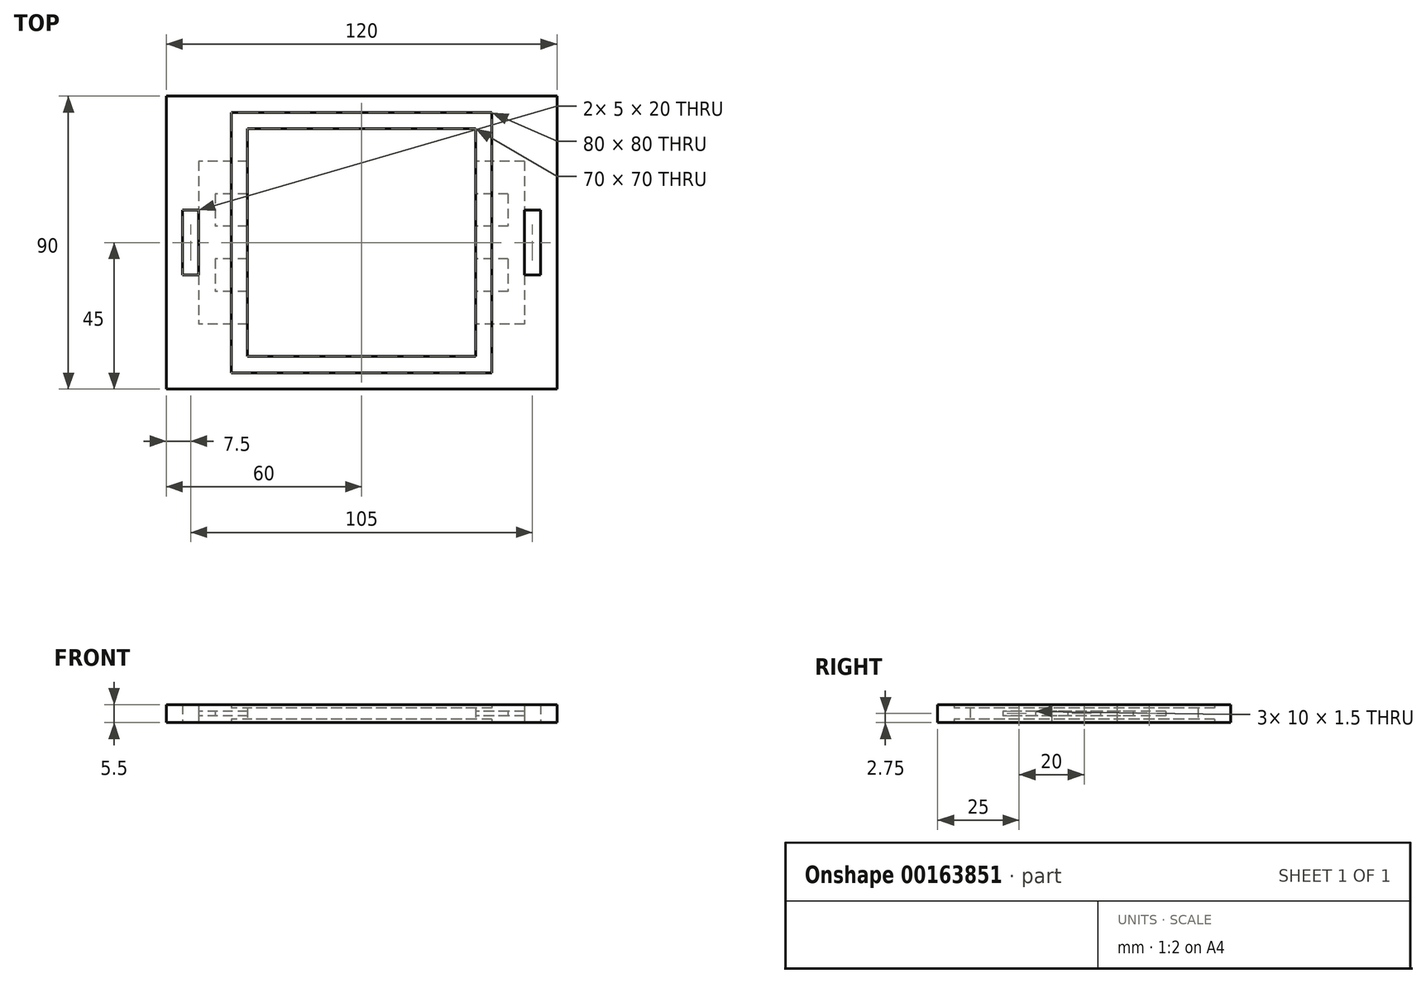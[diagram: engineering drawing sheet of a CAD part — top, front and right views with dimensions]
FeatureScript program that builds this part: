
annotation { "Feature Type Name" : "Feature", "Feature Type Description" : "" }
export const myFeature = defineFeature(function(context is Context, id is Id, definition is map)
    precondition{}
    {
        {
            var Q0;
            Q0=qCreatedBy(makeId("Top.planeOp"),FACE);
            var sketch = newSketch(context, id + "F0", { "sketchPlane" : qUnion([Q0])});
            skLineSegment(sketch, "E0.bottom", {"start": v(60, 45) * mm, "end": v(-60, 45) * mm});
            skLineSegment(sketch, "E0.top", {"start": v(60, -45) * mm, "end": v(-60, -45) * mm});
            skLineSegment(sketch, "E0.left", {"start": v(60, 45) * mm, "end": v(60, -45) * mm});
            skLineSegment(sketch, "E0.right", {"start": v(-60, 45) * mm, "end": v(-60, -45) * mm});
            skPoint(sketch, "E0.middle", {"position": v(0, 0) * mm});
            skLineSegment(sketch, "E1.bottom", {"start": v(35, 35) * mm, "end": v(-35, 35) * mm});
            skLineSegment(sketch, "E1.top", {"start": v(35, -35) * mm, "end": v(-35, -35) * mm});
            skLineSegment(sketch, "E1.left", {"start": v(35, 35) * mm, "end": v(35, -35) * mm});
            skLineSegment(sketch, "E1.right", {"start": v(-35, 35) * mm, "end": v(-35, -35) * mm});
            skLineSegment(sketch, "E2.bottom", {"start": v(40, 40) * mm, "end": v(-40, 40) * mm});
            skLineSegment(sketch, "E2.top", {"start": v(40, -40) * mm, "end": v(-40, -40) * mm});
            skLineSegment(sketch, "E2.left", {"start": v(40, 40) * mm, "end": v(40, -40) * mm});
            skLineSegment(sketch, "E2.right", {"start": v(-40, 40) * mm, "end": v(-40, -40) * mm});
            skLineSegment(sketch, "E3.0", {"start": v(50, 25) * mm, "end": v(35, 25) * mm});
            skLineSegment(sketch, "E4.0", {"start": v(50, -25) * mm, "end": v(35, -25) * mm});
            skLineSegment(sketch, "E5.trimOffspring", {"start": v(-35, 25) * mm, "end": v(-50, 25) * mm});
            skLineSegment(sketch, "E6.trimOffspring", {"start": v(-35, -25) * mm, "end": v(-50, -25) * mm});
            skLineSegment(sketch, "E7.0", {"start": v(-35, 15) * mm, "end": v(-45, 15) * mm});
            skLineSegment(sketch, "E8.0", {"start": v(-35, -15) * mm, "end": v(-45, -15) * mm});
            skLineSegment(sketch, "E9.0", {"start": v(-35, -5) * mm, "end": v(-45, -5) * mm});
            skLineSegment(sketch, "E10.0", {"start": v(-35, 5) * mm, "end": v(-45, 5) * mm});
            skLineSegment(sketch, "E11.0", {"start": v(45, 15) * mm, "end": v(35, 15) * mm});
            skLineSegment(sketch, "E12.0", {"start": v(45, 5) * mm, "end": v(35, 5) * mm});
            skLineSegment(sketch, "E13.0", {"start": v(45, -15) * mm, "end": v(35, -15) * mm});
            skLineSegment(sketch, "E14.0", {"start": v(45, -5) * mm, "end": v(35, -5) * mm});
            skLineSegment(sketch, "E15.0", {"start": v(-50, 25) * mm, "end": v(-50, -25) * mm});
            skLineSegment(sketch, "E16.0", {"start": v(-45, 15) * mm, "end": v(-45, 5) * mm});
            skLineSegment(sketch, "E17.0", {"start": v(50, 25) * mm, "end": v(50, -25) * mm});
            skLineSegment(sketch, "E18.0", {"start": v(45, 15) * mm, "end": v(45, 5) * mm});
            skLineSegment(sketch, "E19.0", {"start": v(55, -10) * mm, "end": v(50, -10) * mm});
            skLineSegment(sketch, "E20.0", {"start": v(55, 10) * mm, "end": v(50, 10) * mm});
            skLineSegment(sketch, "E21.trimOffspring", {"start": v(-50, 10) * mm, "end": v(-55, 10) * mm});
            skLineSegment(sketch, "E22.trimOffspring", {"start": v(-50, -10) * mm, "end": v(-55, -10) * mm});
            skLineSegment(sketch, "E23.0", {"start": v(-55, 10) * mm, "end": v(-55, -10) * mm});
            skLineSegment(sketch, "E24.0", {"start": v(55, 10) * mm, "end": v(55, -10) * mm});
            skLineSegment(sketch, "E25.trimOffspring", {"start": v(45, -5) * mm, "end": v(45, -15) * mm});
            skLineSegment(sketch, "E26.trimOffspring", {"start": v(-45, -5) * mm, "end": v(-45, -15) * mm});
            skSolve(sketch);
        }
        {
            var Q0;
            Q0=makeQuery(id+"F0.imprint","IMPRINT",FACE,{"disambiguationData":[TD([[makeQuery(id+"F0.imprint","IMPRINT",EDGE,{"derivedFrom":sQuery(id+"F0.wireOp",EDGE,"E0.bottom")}),1.0]])]});
            var Q1;
            {var subQ0=sQuery(id+"F0.wireOp",EDGE,"E16.0");Q1=makeQuery(id+"F0.imprint","IMPRINT",FACE,{"disambiguationData":[TD([[makeQuery(id+"F0.imprint","IMPRINT",EDGE,{"derivedFrom":subQ0}),-1.0]])]});}
            var Q2;
            {var subQ4=sQuery(id+"F0.wireOp",EDGE,"E18.0");Q2=makeQuery(id+"F0.imprint","IMPRINT",FACE,{"disambiguationData":[TD([[makeQuery(id+"F0.imprint","IMPRINT",EDGE,{"derivedFrom":subQ4}),1.0]])]});}
            var Q3;
            {var subQ5=sQuery(id+"F0.wireOp",EDGE,"E18.0");Q3=makeQuery(id+"F0.imprint","IMPRINT",FACE,{"disambiguationData":[TD([[makeQuery(id+"F0.imprint","IMPRINT",EDGE,{"derivedFrom":subQ5}),-1.0]])]});}
            var Q4;
            {var subQ5=sQuery(id+"F0.wireOp",EDGE,"E25.trimOffspring");Q4=makeQuery(id+"F0.imprint","IMPRINT",FACE,{"disambiguationData":[TD([[makeQuery(id+"F0.imprint","IMPRINT",EDGE,{"derivedFrom":subQ5}),-1.0]])]});}
            var Q5;
            {var subQ5=sQuery(id+"F0.wireOp",EDGE,"E26.trimOffspring");Q5=makeQuery(id+"F0.imprint","IMPRINT",FACE,{"disambiguationData":[TD([[makeQuery(id+"F0.imprint","IMPRINT",EDGE,{"derivedFrom":subQ5}),1.0]])]});}
            var Q6;
            {var subQ5=sQuery(id+"F0.wireOp",EDGE,"E16.0");Q6=makeQuery(id+"F0.imprint","IMPRINT",FACE,{"disambiguationData":[TD([[makeQuery(id+"F0.imprint","IMPRINT",EDGE,{"derivedFrom":subQ5}),1.0]])]});}
            extrude(context, id + "F1", {"entities" : qUnion([Q0, Q1, Q2, Q3, Q4, Q5, Q6]), "depth" : 2 * mm});
        }
        {
            var Q0;
            Q0=makeQuery(id+"F0.imprint","IMPRINT",FACE,{"disambiguationData":[TD([[makeQuery(id+"F0.imprint","IMPRINT",EDGE,{"derivedFrom":sQuery(id+"F0.wireOp",EDGE,"E0.bottom")}),1.0]])]});
            var Q1;
            {var subQ5=sQuery(id+"F0.wireOp",EDGE,"E26.trimOffspring");Q1=makeQuery(id+"F0.imprint","IMPRINT",FACE,{"disambiguationData":[TD([[makeQuery(id+"F0.imprint","IMPRINT",EDGE,{"derivedFrom":subQ5}),1.0]])]});}
            var Q2;
            {var subQ5=sQuery(id+"F0.wireOp",EDGE,"E16.0");Q2=makeQuery(id+"F0.imprint","IMPRINT",FACE,{"disambiguationData":[TD([[makeQuery(id+"F0.imprint","IMPRINT",EDGE,{"derivedFrom":subQ5}),1.0]])]});}
            var Q3;
            {var subQ5=sQuery(id+"F0.wireOp",EDGE,"E18.0");Q3=makeQuery(id+"F0.imprint","IMPRINT",FACE,{"disambiguationData":[TD([[makeQuery(id+"F0.imprint","IMPRINT",EDGE,{"derivedFrom":subQ5}),-1.0]])]});}
            var Q4;
            {var subQ5=sQuery(id+"F0.wireOp",EDGE,"E25.trimOffspring");Q4=makeQuery(id+"F0.imprint","IMPRINT",FACE,{"disambiguationData":[TD([[makeQuery(id+"F0.imprint","IMPRINT",EDGE,{"derivedFrom":subQ5}),-1.0]])]});}
            extrude(context, id + "F2", {"entities" : qUnion([Q0, Q1, Q2, Q3, Q4]), "operationType" : NewBodyOperationType.ADD, "depth" : 3.5 * mm, "hasSecondDirection" : true, "secondDirectionOppositeDirection" : false, "secondDirectionDepth" : 2 * mm});
        }
        {
            var Q0;
            Q0=makeQuery(id+"F0.imprint","IMPRINT",FACE,{"disambiguationData":[TD([[makeQuery(id+"F0.imprint","IMPRINT",EDGE,{"derivedFrom":sQuery(id+"F0.wireOp",EDGE,"E0.bottom")}),1.0]])]});
            var Q1;
            {var subQ0=sQuery(id+"F0.wireOp",EDGE,"E16.0");Q1=makeQuery(id+"F0.imprint","IMPRINT",FACE,{"disambiguationData":[TD([[makeQuery(id+"F0.imprint","IMPRINT",EDGE,{"derivedFrom":subQ0}),-1.0]])]});}
            var Q2;
            {var subQ4=sQuery(id+"F0.wireOp",EDGE,"E18.0");Q2=makeQuery(id+"F0.imprint","IMPRINT",FACE,{"disambiguationData":[TD([[makeQuery(id+"F0.imprint","IMPRINT",EDGE,{"derivedFrom":subQ4}),1.0]])]});}
            var Q3;
            {var subQ5=sQuery(id+"F0.wireOp",EDGE,"E18.0");Q3=makeQuery(id+"F0.imprint","IMPRINT",FACE,{"disambiguationData":[TD([[makeQuery(id+"F0.imprint","IMPRINT",EDGE,{"derivedFrom":subQ5}),-1.0]])]});}
            var Q4;
            {var subQ5=sQuery(id+"F0.wireOp",EDGE,"E25.trimOffspring");Q4=makeQuery(id+"F0.imprint","IMPRINT",FACE,{"disambiguationData":[TD([[makeQuery(id+"F0.imprint","IMPRINT",EDGE,{"derivedFrom":subQ5}),-1.0]])]});}
            var Q5;
            {var subQ5=sQuery(id+"F0.wireOp",EDGE,"E26.trimOffspring");Q5=makeQuery(id+"F0.imprint","IMPRINT",FACE,{"disambiguationData":[TD([[makeQuery(id+"F0.imprint","IMPRINT",EDGE,{"derivedFrom":subQ5}),1.0]])]});}
            var Q6;
            {var subQ5=sQuery(id+"F0.wireOp",EDGE,"E16.0");Q6=makeQuery(id+"F0.imprint","IMPRINT",FACE,{"disambiguationData":[TD([[makeQuery(id+"F0.imprint","IMPRINT",EDGE,{"derivedFrom":subQ5}),1.0]])]});}
            extrude(context, id + "F3", {"entities" : qUnion([Q0, Q1, Q2, Q3, Q4, Q5, Q6]), "operationType" : NewBodyOperationType.ADD, "depth" : 5.5 * mm, "hasSecondDirection" : true, "secondDirectionOppositeDirection" : false, "secondDirectionDepth" : 3.5 * mm});
        }
        {
            var Q0;
            {var subQ1=sQuery(id+"F0.wireOp",EDGE,"E1.top");Q0=makeQuery(id+"F0.imprint","IMPRINT",FACE,{"disambiguationData":[TD([[makeQuery(id+"F0.imprint","IMPRINT",EDGE,{"derivedFrom":subQ1}),1.0]])]});}
            var Q1;
            {var subQ0=sQuery(id+"F0.wireOp",EDGE,"E6.trimOffspring");var subQ1=sQuery(id+"F0.wireOp",EDGE,"E1.right");var subQ2=makeQuery(id+"F0.imprint","INTERSECT",VERTEX,{"derivedFrom":[subQ1,subQ0]});Q1=makeQuery(id+"F0.imprint","IMPRINT",FACE,{"disambiguationData":[TD([[makeQuery(id+"F0.imprint","IMPRINT",EDGE,{"disambiguationData":[TD([[subQ2,1.0]])],"derivedFrom":subQ1}),-1.0]])]});}
            var Q2;
            {var subQ0=sQuery(id+"F0.wireOp",EDGE,"E8.0");var subQ1=sQuery(id+"F0.wireOp",EDGE,"E1.right");var subQ2=makeQuery(id+"F0.imprint","INTERSECT",VERTEX,{"derivedFrom":[subQ1,subQ0]});Q2=makeQuery(id+"F0.imprint","IMPRINT",FACE,{"disambiguationData":[TD([[makeQuery(id+"F0.imprint","IMPRINT",EDGE,{"disambiguationData":[TD([[subQ2,1.0]])],"derivedFrom":subQ1}),-1.0]])]});}
            var Q3;
            {var subQ0=sQuery(id+"F0.wireOp",EDGE,"E9.0");var subQ1=sQuery(id+"F0.wireOp",EDGE,"E1.right");var subQ2=makeQuery(id+"F0.imprint","INTERSECT",VERTEX,{"derivedFrom":[subQ1,subQ0]});Q3=makeQuery(id+"F0.imprint","IMPRINT",FACE,{"disambiguationData":[TD([[makeQuery(id+"F0.imprint","IMPRINT",EDGE,{"disambiguationData":[TD([[subQ2,1.0]])],"derivedFrom":subQ1}),-1.0]])]});}
            var Q4;
            {var subQ0=sQuery(id+"F0.wireOp",EDGE,"E7.0");var subQ1=sQuery(id+"F0.wireOp",EDGE,"E1.right");var subQ2=makeQuery(id+"F0.imprint","INTERSECT",VERTEX,{"derivedFrom":[subQ1,subQ0]});Q4=makeQuery(id+"F0.imprint","IMPRINT",FACE,{"disambiguationData":[TD([[makeQuery(id+"F0.imprint","IMPRINT",EDGE,{"disambiguationData":[TD([[subQ2,-1.0]])],"derivedFrom":subQ1}),-1.0]])]});}
            var Q5;
            {var subQ0=sQuery(id+"F0.wireOp",EDGE,"E5.trimOffspring");var subQ1=sQuery(id+"F0.wireOp",EDGE,"E1.right");var subQ2=makeQuery(id+"F0.imprint","INTERSECT",VERTEX,{"derivedFrom":[subQ1,subQ0]});Q5=makeQuery(id+"F0.imprint","IMPRINT",FACE,{"disambiguationData":[TD([[makeQuery(id+"F0.imprint","IMPRINT",EDGE,{"disambiguationData":[TD([[subQ2,-1.0]])],"derivedFrom":subQ1}),-1.0]])]});}
            var Q6;
            {var subQ1=sQuery(id+"F0.wireOp",EDGE,"E1.bottom");Q6=makeQuery(id+"F0.imprint","IMPRINT",FACE,{"disambiguationData":[TD([[makeQuery(id+"F0.imprint","IMPRINT",EDGE,{"derivedFrom":subQ1}),-1.0]])]});}
            var Q7;
            {var subQ0=sQuery(id+"F0.wireOp",EDGE,"E3.0");var subQ1=sQuery(id+"F0.wireOp",EDGE,"E1.left");var subQ2=makeQuery(id+"F0.imprint","INTERSECT",VERTEX,{"derivedFrom":[subQ1,subQ0]});Q7=makeQuery(id+"F0.imprint","IMPRINT",FACE,{"disambiguationData":[TD([[makeQuery(id+"F0.imprint","IMPRINT",EDGE,{"disambiguationData":[TD([[subQ2,-1.0]])],"derivedFrom":subQ1}),1.0]])]});}
            var Q8;
            {var subQ0=sQuery(id+"F0.wireOp",EDGE,"E11.0");var subQ1=sQuery(id+"F0.wireOp",EDGE,"E1.left");var subQ2=makeQuery(id+"F0.imprint","INTERSECT",VERTEX,{"derivedFrom":[subQ1,subQ0]});Q8=makeQuery(id+"F0.imprint","IMPRINT",FACE,{"disambiguationData":[TD([[makeQuery(id+"F0.imprint","IMPRINT",EDGE,{"disambiguationData":[TD([[subQ2,-1.0]])],"derivedFrom":subQ1}),1.0]])]});}
            var Q9;
            {var subQ0=sQuery(id+"F0.wireOp",EDGE,"E12.0");var subQ1=sQuery(id+"F0.wireOp",EDGE,"E1.left");var subQ2=makeQuery(id+"F0.imprint","INTERSECT",VERTEX,{"derivedFrom":[subQ1,subQ0]});Q9=makeQuery(id+"F0.imprint","IMPRINT",FACE,{"disambiguationData":[TD([[makeQuery(id+"F0.imprint","IMPRINT",EDGE,{"disambiguationData":[TD([[subQ2,-1.0]])],"derivedFrom":subQ1}),1.0]])]});}
            var Q10;
            {var subQ0=sQuery(id+"F0.wireOp",EDGE,"E13.0");var subQ1=sQuery(id+"F0.wireOp",EDGE,"E1.left");var subQ2=makeQuery(id+"F0.imprint","INTERSECT",VERTEX,{"derivedFrom":[subQ1,subQ0]});Q10=makeQuery(id+"F0.imprint","IMPRINT",FACE,{"disambiguationData":[TD([[makeQuery(id+"F0.imprint","IMPRINT",EDGE,{"disambiguationData":[TD([[subQ2,1.0]])],"derivedFrom":subQ1}),1.0]])]});}
            var Q11;
            {var subQ0=sQuery(id+"F0.wireOp",EDGE,"E4.0");var subQ1=sQuery(id+"F0.wireOp",EDGE,"E1.left");var subQ2=makeQuery(id+"F0.imprint","INTERSECT",VERTEX,{"derivedFrom":[subQ1,subQ0]});Q11=makeQuery(id+"F0.imprint","IMPRINT",FACE,{"disambiguationData":[TD([[makeQuery(id+"F0.imprint","IMPRINT",EDGE,{"disambiguationData":[TD([[subQ2,1.0]])],"derivedFrom":subQ1}),1.0]])]});}
            extrude(context, id + "F4", {"entities" : qUnion([Q0, Q1, Q2, Q3, Q4, Q5, Q6, Q7, Q8, Q9, Q10, Q11]), "operationType" : NewBodyOperationType.ADD, "depth" : 2 * mm, "hasSecondDirection" : true, "secondDirectionOppositeDirection" : false, "secondDirectionDepth" : 1 * mm});
        }
        {
            var Q0;
            {var subQ0=sQuery(id+"F0.wireOp",EDGE,"E7.0");var subQ1=sQuery(id+"F0.wireOp",EDGE,"E1.right");var subQ2=makeQuery(id+"F0.imprint","INTERSECT",VERTEX,{"derivedFrom":[subQ1,subQ0]});Q0=makeQuery(id+"F0.imprint","IMPRINT",FACE,{"disambiguationData":[TD([[makeQuery(id+"F0.imprint","IMPRINT",EDGE,{"disambiguationData":[TD([[subQ2,-1.0]])],"derivedFrom":subQ1}),-1.0]])]});}
            var Q1;
            {var subQ0=sQuery(id+"F0.wireOp",EDGE,"E8.0");var subQ1=sQuery(id+"F0.wireOp",EDGE,"E1.right");var subQ2=makeQuery(id+"F0.imprint","INTERSECT",VERTEX,{"derivedFrom":[subQ1,subQ0]});Q1=makeQuery(id+"F0.imprint","IMPRINT",FACE,{"disambiguationData":[TD([[makeQuery(id+"F0.imprint","IMPRINT",EDGE,{"disambiguationData":[TD([[subQ2,1.0]])],"derivedFrom":subQ1}),-1.0]])]});}
            var Q2;
            {var subQ1=sQuery(id+"F0.wireOp",EDGE,"E1.top");Q2=makeQuery(id+"F0.imprint","IMPRINT",FACE,{"disambiguationData":[TD([[makeQuery(id+"F0.imprint","IMPRINT",EDGE,{"derivedFrom":subQ1}),1.0]])]});}
            var Q3;
            {var subQ0=sQuery(id+"F0.wireOp",EDGE,"E13.0");var subQ1=sQuery(id+"F0.wireOp",EDGE,"E1.left");var subQ2=makeQuery(id+"F0.imprint","INTERSECT",VERTEX,{"derivedFrom":[subQ1,subQ0]});Q3=makeQuery(id+"F0.imprint","IMPRINT",FACE,{"disambiguationData":[TD([[makeQuery(id+"F0.imprint","IMPRINT",EDGE,{"disambiguationData":[TD([[subQ2,1.0]])],"derivedFrom":subQ1}),1.0]])]});}
            var Q4;
            {var subQ0=sQuery(id+"F0.wireOp",EDGE,"E11.0");var subQ1=sQuery(id+"F0.wireOp",EDGE,"E1.left");var subQ2=makeQuery(id+"F0.imprint","INTERSECT",VERTEX,{"derivedFrom":[subQ1,subQ0]});Q4=makeQuery(id+"F0.imprint","IMPRINT",FACE,{"disambiguationData":[TD([[makeQuery(id+"F0.imprint","IMPRINT",EDGE,{"disambiguationData":[TD([[subQ2,-1.0]])],"derivedFrom":subQ1}),1.0]])]});}
            var Q5;
            {var subQ1=sQuery(id+"F0.wireOp",EDGE,"E1.bottom");Q5=makeQuery(id+"F0.imprint","IMPRINT",FACE,{"disambiguationData":[TD([[makeQuery(id+"F0.imprint","IMPRINT",EDGE,{"derivedFrom":subQ1}),-1.0]])]});}
            extrude(context, id + "F5", {"entities" : qUnion([Q0, Q1, Q2, Q3, Q4, Q5]), "operationType" : NewBodyOperationType.ADD, "depth" : 3.5 * mm, "hasSecondDirection" : true, "secondDirectionOppositeDirection" : false, "secondDirectionDepth" : 2 * mm});
        }
        {
            var Q0;
            {var subQ1=sQuery(id+"F0.wireOp",EDGE,"E1.bottom");Q0=makeQuery(id+"F0.imprint","IMPRINT",FACE,{"disambiguationData":[TD([[makeQuery(id+"F0.imprint","IMPRINT",EDGE,{"derivedFrom":subQ1}),-1.0]])]});}
            var Q1;
            {var subQ0=sQuery(id+"F0.wireOp",EDGE,"E5.trimOffspring");var subQ1=sQuery(id+"F0.wireOp",EDGE,"E1.right");var subQ2=makeQuery(id+"F0.imprint","INTERSECT",VERTEX,{"derivedFrom":[subQ1,subQ0]});Q1=makeQuery(id+"F0.imprint","IMPRINT",FACE,{"disambiguationData":[TD([[makeQuery(id+"F0.imprint","IMPRINT",EDGE,{"disambiguationData":[TD([[subQ2,-1.0]])],"derivedFrom":subQ1}),-1.0]])]});}
            var Q2;
            {var subQ0=sQuery(id+"F0.wireOp",EDGE,"E7.0");var subQ1=sQuery(id+"F0.wireOp",EDGE,"E1.right");var subQ2=makeQuery(id+"F0.imprint","INTERSECT",VERTEX,{"derivedFrom":[subQ1,subQ0]});Q2=makeQuery(id+"F0.imprint","IMPRINT",FACE,{"disambiguationData":[TD([[makeQuery(id+"F0.imprint","IMPRINT",EDGE,{"disambiguationData":[TD([[subQ2,-1.0]])],"derivedFrom":subQ1}),-1.0]])]});}
            var Q3;
            {var subQ0=sQuery(id+"F0.wireOp",EDGE,"E9.0");var subQ1=sQuery(id+"F0.wireOp",EDGE,"E1.right");var subQ2=makeQuery(id+"F0.imprint","INTERSECT",VERTEX,{"derivedFrom":[subQ1,subQ0]});Q3=makeQuery(id+"F0.imprint","IMPRINT",FACE,{"disambiguationData":[TD([[makeQuery(id+"F0.imprint","IMPRINT",EDGE,{"disambiguationData":[TD([[subQ2,1.0]])],"derivedFrom":subQ1}),-1.0]])]});}
            var Q4;
            {var subQ0=sQuery(id+"F0.wireOp",EDGE,"E8.0");var subQ1=sQuery(id+"F0.wireOp",EDGE,"E1.right");var subQ2=makeQuery(id+"F0.imprint","INTERSECT",VERTEX,{"derivedFrom":[subQ1,subQ0]});Q4=makeQuery(id+"F0.imprint","IMPRINT",FACE,{"disambiguationData":[TD([[makeQuery(id+"F0.imprint","IMPRINT",EDGE,{"disambiguationData":[TD([[subQ2,1.0]])],"derivedFrom":subQ1}),-1.0]])]});}
            var Q5;
            {var subQ0=sQuery(id+"F0.wireOp",EDGE,"E6.trimOffspring");var subQ1=sQuery(id+"F0.wireOp",EDGE,"E1.right");var subQ2=makeQuery(id+"F0.imprint","INTERSECT",VERTEX,{"derivedFrom":[subQ1,subQ0]});Q5=makeQuery(id+"F0.imprint","IMPRINT",FACE,{"disambiguationData":[TD([[makeQuery(id+"F0.imprint","IMPRINT",EDGE,{"disambiguationData":[TD([[subQ2,1.0]])],"derivedFrom":subQ1}),-1.0]])]});}
            var Q6;
            {var subQ1=sQuery(id+"F0.wireOp",EDGE,"E1.top");Q6=makeQuery(id+"F0.imprint","IMPRINT",FACE,{"disambiguationData":[TD([[makeQuery(id+"F0.imprint","IMPRINT",EDGE,{"derivedFrom":subQ1}),1.0]])]});}
            var Q7;
            {var subQ0=sQuery(id+"F0.wireOp",EDGE,"E4.0");var subQ1=sQuery(id+"F0.wireOp",EDGE,"E1.left");var subQ2=makeQuery(id+"F0.imprint","INTERSECT",VERTEX,{"derivedFrom":[subQ1,subQ0]});Q7=makeQuery(id+"F0.imprint","IMPRINT",FACE,{"disambiguationData":[TD([[makeQuery(id+"F0.imprint","IMPRINT",EDGE,{"disambiguationData":[TD([[subQ2,1.0]])],"derivedFrom":subQ1}),1.0]])]});}
            var Q8;
            {var subQ0=sQuery(id+"F0.wireOp",EDGE,"E13.0");var subQ1=sQuery(id+"F0.wireOp",EDGE,"E1.left");var subQ2=makeQuery(id+"F0.imprint","INTERSECT",VERTEX,{"derivedFrom":[subQ1,subQ0]});Q8=makeQuery(id+"F0.imprint","IMPRINT",FACE,{"disambiguationData":[TD([[makeQuery(id+"F0.imprint","IMPRINT",EDGE,{"disambiguationData":[TD([[subQ2,1.0]])],"derivedFrom":subQ1}),1.0]])]});}
            var Q9;
            {var subQ0=sQuery(id+"F0.wireOp",EDGE,"E12.0");var subQ1=sQuery(id+"F0.wireOp",EDGE,"E1.left");var subQ2=makeQuery(id+"F0.imprint","INTERSECT",VERTEX,{"derivedFrom":[subQ1,subQ0]});Q9=makeQuery(id+"F0.imprint","IMPRINT",FACE,{"disambiguationData":[TD([[makeQuery(id+"F0.imprint","IMPRINT",EDGE,{"disambiguationData":[TD([[subQ2,-1.0]])],"derivedFrom":subQ1}),1.0]])]});}
            var Q10;
            {var subQ0=sQuery(id+"F0.wireOp",EDGE,"E11.0");var subQ1=sQuery(id+"F0.wireOp",EDGE,"E1.left");var subQ2=makeQuery(id+"F0.imprint","INTERSECT",VERTEX,{"derivedFrom":[subQ1,subQ0]});Q10=makeQuery(id+"F0.imprint","IMPRINT",FACE,{"disambiguationData":[TD([[makeQuery(id+"F0.imprint","IMPRINT",EDGE,{"disambiguationData":[TD([[subQ2,-1.0]])],"derivedFrom":subQ1}),1.0]])]});}
            var Q11;
            {var subQ0=sQuery(id+"F0.wireOp",EDGE,"E3.0");var subQ1=sQuery(id+"F0.wireOp",EDGE,"E1.left");var subQ2=makeQuery(id+"F0.imprint","INTERSECT",VERTEX,{"derivedFrom":[subQ1,subQ0]});Q11=makeQuery(id+"F0.imprint","IMPRINT",FACE,{"disambiguationData":[TD([[makeQuery(id+"F0.imprint","IMPRINT",EDGE,{"disambiguationData":[TD([[subQ2,-1.0]])],"derivedFrom":subQ1}),1.0]])]});}
            extrude(context, id + "F6", {"entities" : qUnion([Q0, Q1, Q2, Q3, Q4, Q5, Q6, Q7, Q8, Q9, Q10, Q11]), "operationType" : NewBodyOperationType.ADD, "depth" : 4.5 * mm, "hasSecondDirection" : true, "secondDirectionOppositeDirection" : false, "secondDirectionDepth" : 3.5 * mm});
        }
    });
